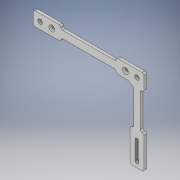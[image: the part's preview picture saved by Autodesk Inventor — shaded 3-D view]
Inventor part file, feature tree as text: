
AUTODESK INVENTOR PART (.ipt)
format: ipt  version: 2019 (Build 230136000, 136)  size: 206,848 bytes
history: native  units: mm
features: extrude x3, sketch x3, plane x2, mirror x2, fillet x2, hole x1
ambient origin geometry x8: Origin, YZ Plane, XZ Plane, XY Plane, X Axis, Y Axis, Z Axis, Center Point
bodies: Solid1 (feature_tree)
feature tree (13):
  extrude  "Extrusion1"  Depth=15.0mm
  hole  "Hole1"  [1 undecoded]
  extrude  "Extrusion2"  Depth=3.0mm TaperAngle=0.0deg
  plane  "Work Plane1"
  mirror  "Mirror1"
  fillet  "Fillet1"  Radius=80.0mm
  extrude  "Extrusion3"  Depth=2.0mm
  plane  "Work Plane2"
  mirror  "Mirror2"
  fillet  "Fillet2"  Radius=10.0mm
  sketch  "Sketch2"  dims[d0=120.0mm d1=15.0mm]
  sketch  "Sketch3"  dims[d2=5.0mm d3=7.5mm]
  sketch  "Sketch4"  dims[d4=7.5mm d5=3.0mm d6=0.0mm d7=80.0mm d8=3.3mm d9=6.0mm d10=6.5mm d11=2.0mm d12=90.0deg d13=36.25mm d14=0.0mm d15=2.0mm d16=10.0mm d17=10.0mm d18=4.0mm d19=3.0mm d20=0.0mm d21=15.0mm d23=15.0mm d24=70.0mm d25=4.0mm d26=20.0mm d27=4.0mm d28=10.0mm d29=10.0mm d30=10.0mm d31=0.0mm d32=2.0mm]
note: 1 required parameter value undecoded (feature->parameter linkage not recoverable at this tier; creation-order binding heuristic only, values carry confidence <= 0.55)
